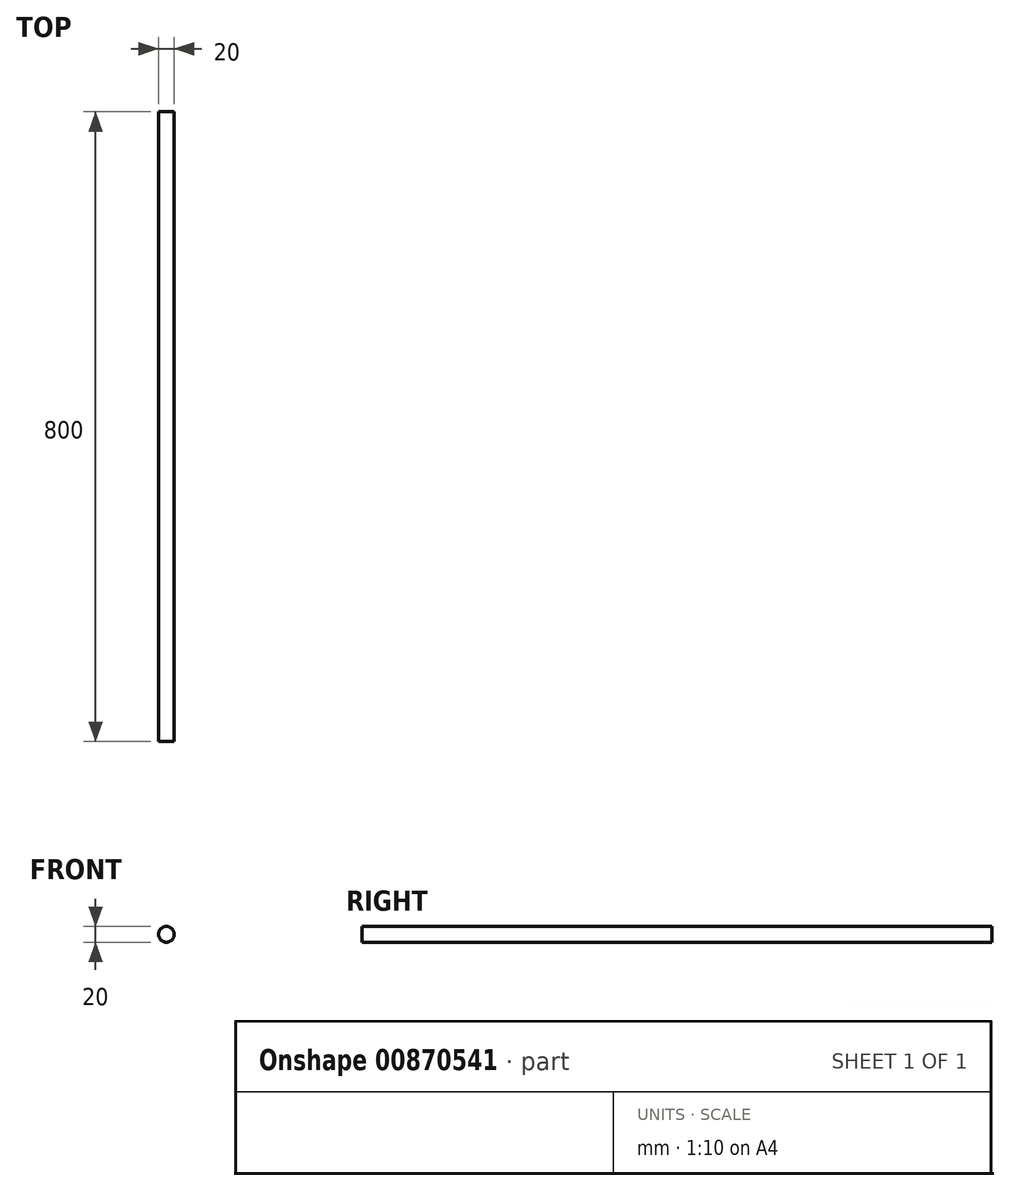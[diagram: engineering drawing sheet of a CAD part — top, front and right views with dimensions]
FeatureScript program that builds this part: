
annotation { "Feature Type Name" : "Feature", "Feature Type Description" : "" }
export const myFeature = defineFeature(function(context is Context, id is Id, definition is map)
    precondition{}
    {
        {
            var Q0;
            Q0=qCreatedBy(makeId("Front.planeOp"),FACE);
            var sketch = newSketch(context, id + "F0", { "sketchPlane" : qUnion([Q0])});
            skCircle(sketch, "E0", {"center": v(0, 0) * mm, "radius": 10 * mm});
            skSolve(sketch);
        }
        {
            var Q0;
            Q0 = qSketchRegion(id + "F0", true);
            extrude(context, id + "F1", {"entities" : qUnion([Q0]), "depth" : 800 * mm, "offsetDistance" : 25 * mm});
        }
    });
